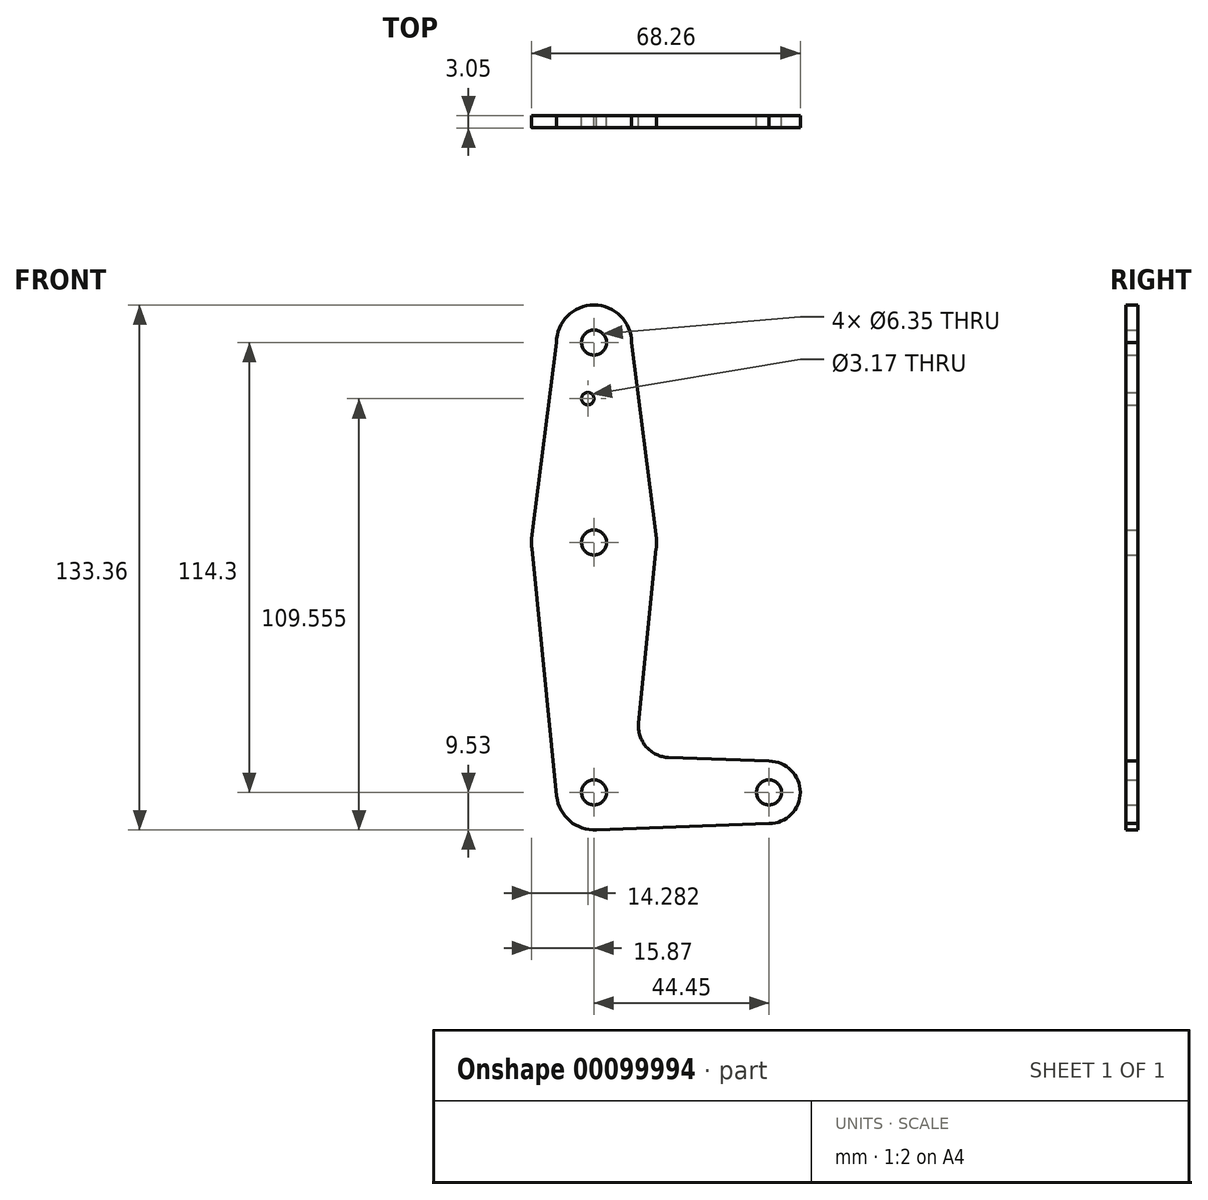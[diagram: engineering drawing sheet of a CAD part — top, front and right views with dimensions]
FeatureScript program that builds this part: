
annotation { "Feature Type Name" : "Feature", "Feature Type Description" : "" }
export const myFeature = defineFeature(function(context is Context, id is Id, definition is map)
    precondition{}
    {
        {
            var Q0;
            Q0=qCreatedBy(makeId("Front.planeOp"),FACE);
            var sketch = newSketch(context, id + "F0", { "sketchPlane" : qUnion([Q0])});
            skLineSegment(sketch, "E0", {"start": v(0, 0) * mm, "end": v(0, 114.3) * mm});
            skLineSegment(sketch, "E1", {"start": v(0, 0) * mm, "end": v(44.45, 0) * mm});
            skCircle(sketch, "E2", {"center": v(0, 114.3) * mm, "radius": 9.53 * mm});
            skCircle(sketch, "E3", {"center": v(0, 63.5) * mm, "radius": 15.88 * mm});
            skCircle(sketch, "E4", {"center": v(0, 0) * mm, "radius": 9.53 * mm});
            skCircle(sketch, "E5", {"center": v(44.45, 0) * mm, "radius": 7.94 * mm});
            skLineSegment(sketch, "E6", {"start": v(-9.52, 114.3) * mm, "end": v(-15.75, 65.5) * mm});
            skLineSegment(sketch, "E7", {"start": v(9.53, 114.3) * mm, "end": v(15.75, 65.5) * mm});
            skLineSegment(sketch, "E8", {"start": v(0, -9.52) * mm, "end": v(44.45, -7.94) * mm});
            skCircle(sketch, "E9", {"center": v(0, 114.3) * mm, "radius": 3.18 * mm});
            skCircle(sketch, "E10", {"center": v(0, 63.5) * mm, "radius": 3.18 * mm});
            skCircle(sketch, "E11", {"center": v(0, 0) * mm, "radius": 3.18 * mm});
            skCircle(sketch, "E12", {"center": v(44.45, 0) * mm, "radius": 3.18 * mm});
            skLineSegment(sketch, "E13", {"start": v(15.8, 61.91) * mm, "end": v(11.34, 17.6) * mm});
            skLineSegment(sketch, "E14", {"start": v(44.45, 7.94) * mm, "end": v(18.97, 8.85) * mm});
            skCircle(sketch, "E15", {"center": v(-1.59, 100.03) * mm, "radius": 1.59 * mm});
            skPoint(sketch, "E16.newPointA", {"position": v(0, 9.53) * mm});
            skArc(sketch, "E16.filletArc", {"start": v(11.34, 17.6) * mm, "mid": v(13.26, 11.57) * mm, "end": v(18.97, 8.85) * mm});
            skLineSegment(sketch, "E17", {"start": v(-15.8, 61.91) * mm, "end": v(-9.48, -0.95) * mm});
            skSolve(sketch);
        }
        {
            var Q0;
            Q0 = qSketchRegion(id + "F0", true);
            var Q1;
            {var subQ0=sQuery(id+"F0.wireOp",EDGE,"E11");var subQ1=sQuery(id+"F0.wireOp",EDGE,"E0");var subQ2=makeQuery(id+"F0.imprint","INTERSECT",VERTEX,{"derivedFrom":[subQ1,subQ0]});Q1=makeQuery(id+"F0.imprint","IMPRINT",FACE,{"disambiguationData":[TD([[makeQuery(id+"F0.imprint","IMPRINT",EDGE,{"disambiguationData":[TD([[subQ2,-1.0]])],"derivedFrom":subQ1}),-1.0]])]});}
            extrude(context, id + "F1", {"entities" : qUnion([Q0, Q1]), "depth" : 3.05 * mm});
        }
    });
